# Revit family: Faucet-Touchless-Lavatory-KOHLER-Components-K-103MT86
name_source: partatom
category: Plumbing Fixtures
units: mm (PartAtom-declared; Revit-internal decimal feet)

## family parameters
Cut with Voids When Loaded = No
Host = Face
OmniClass Number = 23.31.11.00
OmniClass Title = Faucets
Part Type = Normal
Room Calculation Point = No
Round Connector Dimension = Use Diameter
Shared = No

## types (5) — shared parameters
ADA Compliant = No
Apparent Load = 0 VA
Assembly Code = D2010
CW Connection = Yes
Cold Water Inlet = Cold Water Inlet
Date Modified = 01/14/2024
Default Elevation = 36"
Drain Included = Yes
Electrical Connector = Yes
Electrical Note = One Dedicated Circuit Required
HW Connection = No
Height = 11 15/16"
Hot Water Inlet = Hot Water Inlet
Length = 5 3/4"
Manufacturer = Kohler Co.
Master Format 2014 = 22 41 39
Master Format 2014 Name = Residential Faucets, Supplies, and Trim
Material = Premium Metal Construction
Pressure = 0.00 psi
Product Documentation Link = https://www.us.kohler.com
Product Name = Components
Product Page URL = http://www.us.kohler.com
Spout Reach = 5 3/4"
Tempered Water Inlet = Tempered Water Inlet
URL = https://www.us.kohler.com
Vent Connection = No
Voltage = 220 V
Waste Connection = No
Waste Water Outlet = Waste Water Outlet
WaterSense Certified = No
Width = 2 3/8"

## per-type parameters (varying)
| type | Description | Finish | Flow Rate | Model | Type |
| 0.35 GPM, CP-Polished Chrome | TB Medium Height Deck Mount 0.35GPM - Base No Power Supply (AC) - Cold Only | Kohler-Metal-CP-Polished_Chrome | 0 GPM | K-103MT86-SATA-CP | 5 |
| 0.5 GPM, CP-Polished Chrome | TB Medium Height Deck Mount 0.5GPM - Base No Power Supply (AC) - Cold Only | Kohler-Metal-CP-Polished_Chrome | 1 GPM | K-103MT86-SANA-CP | 4 |
| 0.5 GPM, 2MB-Vibrant Brushed Moderne Brass | TB Medium Height Deck Mount 0.5GPM - Base No Power Supply (AC) - Cold Only | Kohler-Metal-2MB-Vibrant_Brushed_Moderne_Brass | 1 GPM | K-103MT86-SANA-2MB | 1 |
| 0.5 GPM, BL-Matte Black | TB Medium Height Deck Mount 0.5GPM - Base No Power Supply (AC) - Cold Only | Kohler-Metal-BL-Matte_Black | 1 GPM | K-103MT86-SANA-BL | 2 |
| 0.5 GPM, BN-Vibrant Brushed Nickel | TB Medium Height Deck Mount 0.5GPM - Base No Power Supply (AC) - Cold Only | Kohler-Metal-BN-Vibrant_Brushed_Nickel | 1 GPM | K-103MT86-SANA-BN | 3 |

## geometry (parser evidence)
native form markers: Sweep x5
no freeform markers — native parametric forms only
